# Revit family: PRD_FrankeWS_SoapDpnsrs_SoapDispenser_SD110
name_source: partatom
category: Specialty Equipment
revit_build: Autodesk Revit 2018 (Build: 20190510_1515(x64)
units: mm (PartAtom-declared; Revit-internal decimal feet)

## family parameters
Cut with Voids When Loaded = No
Host = Face
OmniClass Number = 23.40.20.21.34
OmniClass Title = Soap Holders, Dispensers
Part Type = Normal
Room Calculation Point = No
Round Connector Dimension = Use Diameter
Shared = No

## types (1)
- SD110
    AssetType = Fixed
    BIMObjectName = PRD_AR_SoapDispensers_SoapDispenser_SD110
    Category = Pr_40_70_22_81, Soap dispensers
    Color = Chrome
    Default Elevation = 1100 mm
    Description = Soap dispenser for wall mounting and re-filling from Serviceroom behind the wall, high polished chromated brass, requires 18 mm drilling hole, 3/8inch. thread, spout not movable, suitable for liquid soaps and lotions, without soap tank (can be directly connected to soap can), for filling from behind the wall.
    DurationUnit = year
    Features = brass, chromed, counter top mounting, 50x50x634 mm (WxHxD)
    Finish = High polished
    Form = Wall mounted
    GrossWeight = 0.00 kg
    IfcExportAs = IfcFurnitureType
    IfcExportType = NOTDEFINED
    MainColor = Stainless steel
    Manufacturer = KWC Group AG
    ManufacturerName = KWC Group AG
    ManufacturerURL = www.kwc.com
    Material = Brass
    MaterialsBody = Brass
    MaterialsFinishAndColour = High polished chromated brass
    Model = SD110
    ModelNumber = 2000102699
    ModelReference = SD110
    NBSDescription = Soap dispensers
    NBSReference = 45-35-72/358
    Name = Soap dispenser SD110
    NetWeight = 0.00 kg
    NominalDepth = 634 mm  [stored 2.08005 ft]
    NominalHeight = 50 mm  [stored 0.164042 ft]
    NominalLength = 50 mm  [stored 0.164042 ft]
    NominalWidth = 50 mm  [stored 0.164042 ft]
    Operation = Manual
    ProductInformation = https://pim.kwc.com
    Shape = Cylindrical
    Size = 50 x 50 x 634 mm
    SoapDispenserMaterial = PRD_AR_ChromatedBrass_HighPolished
    Style = Soap dispenser
    TypeOfConsumable = Liquid soap
    URL = www.kwc.com
    Uniclass2015Code = Pr_40_70_22_81
    Uniclass2015Title = Soap dispensers
    Uniclass2015Version = Products v1.5
    Version = 1
    WarrantyDurationUnit = year

note: [stored X ft] marks values corroborated as IEEE doubles in the binary element streams (Revit-internal decimal feet)

## geometry (parser evidence)
native form markers: Sweep x1
no freeform markers — native parametric forms only
